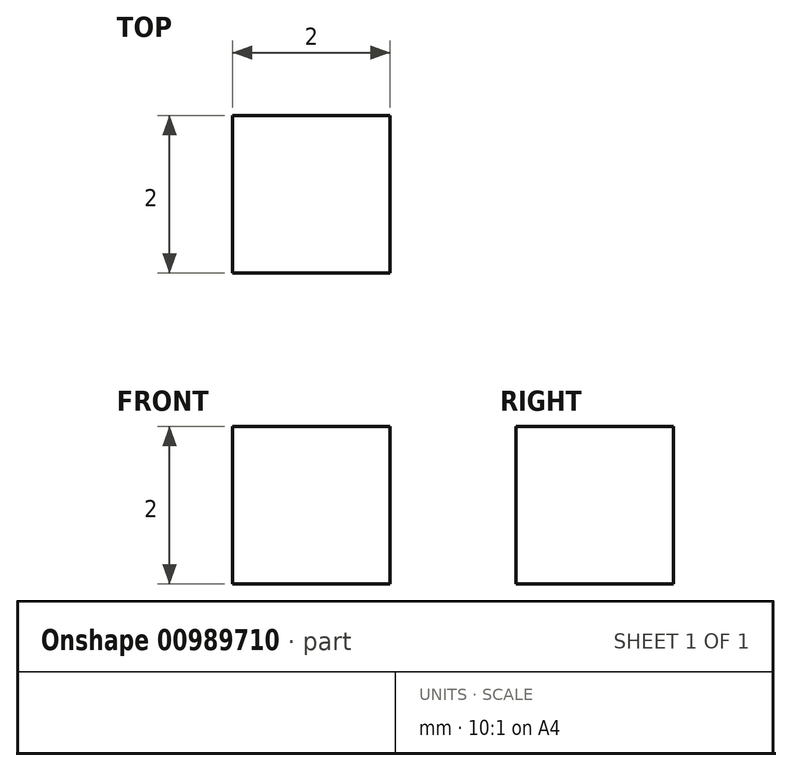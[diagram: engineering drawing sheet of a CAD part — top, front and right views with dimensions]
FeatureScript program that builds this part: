
annotation { "Feature Type Name" : "Feature", "Feature Type Description" : "" }
export const myFeature = defineFeature(function(context is Context, id is Id, definition is map)
    precondition{}
    {
        {
            var Q0;
            Q0=qCreatedBy(makeId("Front.planeOp"),FACE);
            var sketch = newSketch(context, id + "F0", { "sketchPlane" : qUnion([Q0])});
            skLineSegment(sketch, "E0.bottom", {"start": v(0, 0) * mm, "end": v(2, 0) * mm});
            skLineSegment(sketch, "E0.top", {"start": v(0, 2) * mm, "end": v(2, 2) * mm});
            skLineSegment(sketch, "E0.left", {"start": v(0, 0) * mm, "end": v(0, 2) * mm});
            skLineSegment(sketch, "E0.right", {"start": v(2, 0) * mm, "end": v(2, 2) * mm});
            skSolve(sketch);
        }
        {
            var Q0;
            Q0 = qSketchRegion(id + "F0", true);
            extrude(context, id + "F1", {"entities" : qUnion([Q0]), "endBound" : BoundingType.SYMMETRIC, "depth" : 2 * mm, "offsetDistance" : 25 * mm});
        }
    });
